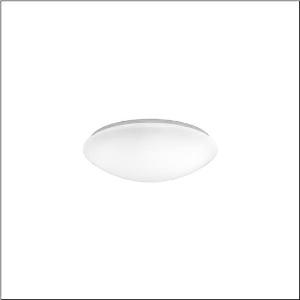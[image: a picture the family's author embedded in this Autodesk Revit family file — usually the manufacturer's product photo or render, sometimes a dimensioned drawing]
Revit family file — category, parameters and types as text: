
# Revit family: round_31_b_5pja012001a
name_source: partatom
category: Lighting Fixtures
units: mm (PartAtom-declared; Revit-internal decimal feet)

## family parameters
Cut with Voids When Loaded = No
Host = Face
Light Source = No
Part Type = Normal
Room Calculation Point = No
Round Connector Dimension = Use Diameter
Shared = No

## types (1)
- Round 31 B (1 x LED, 1800 lm, 15 W, 3000K)
    Apparent Load = 15 VA
    CIE Flux Codes = 42 71 89 88 100
    Color Rendering = 80
    Color Temperature = 3000K
    Default Elevation = 1800 mm  [stored 5.90551 ft]
    Description = Round 31 B, wall and ceiling luminaire, primary optical cover: enclosure, of PMMA, light emission: direct distribution, primary light characteristic: symmetric, installation type: surface-mounted, LED, rated luminous flux: 1.800lm, luminous efficacy: 120lm/W, light colour: 830, colour temperature: 3000K, with terminal, 3+2-pole, max. 2.5mm², mains connection: 230V, AC, 50/60Hz, rated input power: 15W, luminaire housing, round, of steel, white, diameter: 290mm, height: 85mm, protection rating (complete): IP40, insulation class (complete): insulation class I (protective earthing), certification: CE, impact resistance: IK02, permissible operating ambient temperature: -20..+25°C, packaging unit: 1 piece
    Height = 85 mm
    Lamp = 1 x LED
    Lamp Light Flux = 1800 lm
    Lamp Power = 15 W
    Lamp count = 1
    Length = 290 mm
    Luminous efficacy = 120 lm/W
    Manufacturer = Siteco
    ModVariant = No
    Model = 5PJA012001A
    Mounting Place = Ceiling
    Mounting Type = Surface mounted
    Number of Poles = 1
    OnlyDefault = Yes
    Power Factor = 1
    Product Name = Round 31 B
    Product group = wall and ceiling luminaire
    ProductGroupID = 301
    Protection Class = Protection class I
    Protection Degree = IP 40
    RLX_Detail_Level = 1
    RLX_Emergency_Light_Flux = 0 lm
    RLX_Emergency_Type = 0
    RLX_Emergency_Type_DB = No
    RlxData = <blob elided: 9237 chars, md5=8ee7804d>
    Socket = socket
    Standby Power = 0 W
    System Light Flux = 1800 lm
    System Power = 15 W
    Type Comments = Product without accessories
    Type Image = l_1258346.jpg
    URL = http://relux.com
    VarID = ---
    Voltage = 0 V
    Weight = 0.00 kg
    Width = 0 mm  [stored 0 ft]

note: [stored X ft] marks values corroborated as IEEE doubles in the binary element streams (Revit-internal decimal feet)

## geometry (parser evidence)
native form markers: Sweep x12
no freeform markers — native parametric forms only
